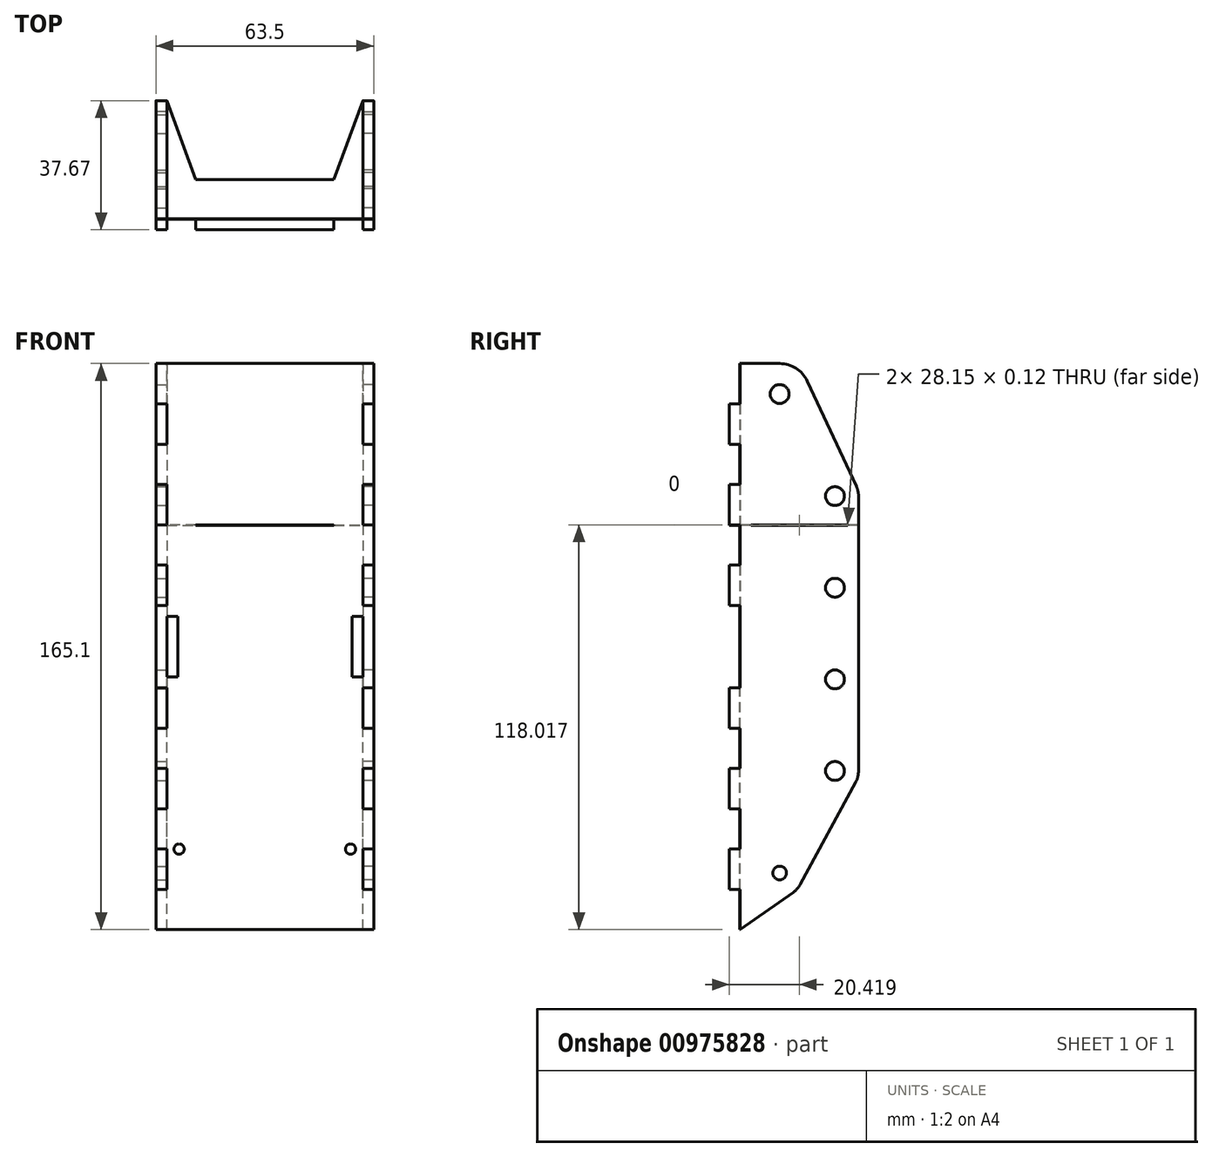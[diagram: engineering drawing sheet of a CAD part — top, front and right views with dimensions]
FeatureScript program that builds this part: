
annotation { "Feature Type Name" : "Feature", "Feature Type Description" : "" }
export const myFeature = defineFeature(function(context is Context, id is Id, definition is map)
    precondition{}
    {
        {
            assignVariable(context, id + "F0", {"name" : "Thickness", "anyValue" : .125});
        }
        {
            var Q0;
            Q0=qCreatedBy(makeId("Front.planeOp"),FACE);
            var sketch = newSketch(context, id + "F1", { "sketchPlane" : qUnion([Q0])});
            skLineSegment(sketch, "E0", {"start": v(0, 0) * mm, "end": v(0, 49.56) * mm, "construction": true});
            skLineSegment(sketch, "E1", {"start": v(0, 0) * mm, "end": v(-25, 0) * mm, "construction": true});
            skCircle(sketch, "E2", {"center": v(-25, 0) * mm, "radius": 1.5 * mm, "construction": true});
            skLineSegment(sketch, "E3", {"start": v(0, -7) * mm, "end": v(-39.83, -7) * mm, "construction": true});
            skLineSegment(sketch, "E4", {"start": v(0, 141.6) * mm, "end": v(-22.22, 141.6) * mm, "construction": true});
            skLineSegment(sketch, "E5", {"start": v(-22.23, 141.6) * mm, "end": v(-22.22, -23.51) * mm, "construction": true});
            skLineSegment(sketch, "E6", {"start": v(-22.22, -23.51) * mm, "end": v(0, -23.5) * mm, "construction": true});
            skSolve(sketch);
        }
        {
            var Q0;
            Q0=qCreatedBy(makeId("Right.planeOp"),FACE);
            var sketch = newSketch(context, id + "F2", { "sketchPlane" : qUnion([Q0])});
            skLineSegment(sketch, "E7", {"start": v(0, -7) * mm, "end": v(11.5, -7) * mm, "construction": true});
            skCircle(sketch, "E8", {"center": v(11.5, -7) * mm, "radius": 2 * mm});
            skCircle(sketch, "E9", {"center": v(11.5, 132.7) * mm, "radius": 2.75 * mm});
            skSolve(sketch);
        }
        {
            var Q0;
            Q0=qCreatedBy(makeId("Front.planeOp"),FACE);
            var sketch = newSketch(context, id + "F3", { "sketchPlane" : qUnion([Q0])});
            skLineSegment(sketch, "E10", {"start": v(0, 141.6) * mm, "end": v(-31.75, 141.6) * mm, "construction": true});
            skLineSegment(sketch, "E11", {"start": v(0, -23.51) * mm, "end": v(-31.75, -23.51) * mm});
            skLineSegment(sketch, "E12", {"start": v(-31.75, -23.51) * mm, "end": v(-31.75, -11.76) * mm});
            skLineSegment(sketch, "E13", {"start": v(-31.75, -11.76) * mm, "end": v(-28.57, -11.76) * mm});
            skLineSegment(sketch, "E14", {"start": v(-28.57, -11.76) * mm, "end": v(-28.57, 0) * mm});
            skLineSegment(sketch, "E15", {"start": v(-28.57, 0) * mm, "end": v(-31.75, 0) * mm});
            skLineSegment(sketch, "E16", {"start": v(0, -23.51) * mm, "end": v(0, 141.6) * mm, "construction": true});
            skLineSegment(sketch, "E17", {"start": v(0, 59.04) * mm, "end": v(-66.34, 59.04) * mm, "construction": true});
            skLineSegment(sketch, "E18", {"start": v(-31.75, 59.04) * mm, "end": v(-31.75, 47.02) * mm});
            skLineSegment(sketch, "E19.1.0.0", {"start": v(-28.57, 23.51) * mm, "end": v(-31.75, 23.51) * mm});
            skLineSegment(sketch, "E19.1.0.1", {"start": v(-28.57, 11.76) * mm, "end": v(-28.57, 23.51) * mm});
            skLineSegment(sketch, "E19.1.0.2", {"start": v(-31.75, 11.76) * mm, "end": v(-28.57, 11.76) * mm});
            skLineSegment(sketch, "E19.1.0.3", {"start": v(-31.75, 0) * mm, "end": v(-31.75, 11.76) * mm});
            skLineSegment(sketch, "E19.2.0.0", {"start": v(-28.58, 47.02) * mm, "end": v(-31.75, 47.02) * mm});
            skLineSegment(sketch, "E19.2.0.1", {"start": v(-28.57, 35.27) * mm, "end": v(-28.57, 47.02) * mm});
            skLineSegment(sketch, "E19.2.0.2", {"start": v(-31.75, 35.27) * mm, "end": v(-28.58, 35.27) * mm});
            skLineSegment(sketch, "E19.2.0.3", {"start": v(-31.75, 23.51) * mm, "end": v(-31.75, 35.27) * mm});
            skLineSegment(sketch, "E19.direction1", {"start": v(-31.75, -23.51) * mm, "end": v(-31.75, 0) * mm, "construction": true});
            skLineSegment(sketch, "E20.MirrorCS", {"start": v(-31.75, 141.6) * mm, "end": v(-31.75, 129.84) * mm});
            skLineSegment(sketch, "E21.MirrorCS", {"start": v(-28.57, 118.08) * mm, "end": v(-31.75, 118.08) * mm});
            skLineSegment(sketch, "E22.MirrorCS", {"start": v(-28.58, 71.06) * mm, "end": v(-31.75, 71.06) * mm});
            skLineSegment(sketch, "E23.MirrorCS", {"start": v(-31.75, 94.57) * mm, "end": v(-31.75, 82.81) * mm});
            skLineSegment(sketch, "E24.MirrorCS", {"start": v(-31.75, 118.08) * mm, "end": v(-31.75, 106.33) * mm});
            skLineSegment(sketch, "E25.MirrorCS", {"start": v(-31.75, 129.84) * mm, "end": v(-28.57, 129.84) * mm});
            skLineSegment(sketch, "E26.MirrorCS", {"start": v(-28.57, 129.84) * mm, "end": v(-28.57, 118.08) * mm});
            skLineSegment(sketch, "E27.MirrorCS", {"start": v(-28.57, 82.81) * mm, "end": v(-28.57, 71.06) * mm});
            skLineSegment(sketch, "E28.MirrorCS", {"start": v(-31.75, 82.81) * mm, "end": v(-28.58, 82.81) * mm});
            skLineSegment(sketch, "E29.MirrorCS", {"start": v(-31.75, 106.33) * mm, "end": v(-28.57, 106.33) * mm});
            skLineSegment(sketch, "E30.MirrorCS", {"start": v(-28.57, 106.33) * mm, "end": v(-28.57, 94.57) * mm});
            skLineSegment(sketch, "E31.MirrorCS", {"start": v(-28.57, 94.57) * mm, "end": v(-31.75, 94.57) * mm});
            skLineSegment(sketch, "E32.MirrorCS", {"start": v(0, 141.6) * mm, "end": v(-31.75, 141.6) * mm});
            skLineSegment(sketch, "E33.MirrorCS", {"start": v(-31.75, 59.04) * mm, "end": v(-31.75, 71.06) * mm});
            skLineSegment(sketch, "E34.bottom", {"start": v(-28.58, 67.89) * mm, "end": v(-25.4, 67.89) * mm});
            skLineSegment(sketch, "E34.top", {"start": v(-28.58, 50.2) * mm, "end": v(-25.4, 50.2) * mm});
            skLineSegment(sketch, "E34.left", {"start": v(-28.58, 67.89) * mm, "end": v(-28.58, 50.2) * mm});
            skLineSegment(sketch, "E34.right", {"start": v(-25.4, 67.89) * mm, "end": v(-25.4, 50.2) * mm});
            skPoint(sketch, "E35", {"position": v(-28.58, 59.04) * mm});
            skLineSegment(sketch, "E36.MirrorCS", {"start": v(28.57, 23.51) * mm, "end": v(31.75, 23.51) * mm});
            skLineSegment(sketch, "E37.MirrorCS", {"start": v(31.75, 35.27) * mm, "end": v(28.58, 35.27) * mm});
            skLineSegment(sketch, "E38.MirrorCS", {"start": v(28.58, 71.06) * mm, "end": v(31.75, 71.06) * mm});
            skLineSegment(sketch, "E39.MirrorCS", {"start": v(31.75, -23.51) * mm, "end": v(31.75, -11.76) * mm});
            skLineSegment(sketch, "E40.MirrorCS", {"start": v(28.57, 0) * mm, "end": v(31.75, 0) * mm});
            skLineSegment(sketch, "E41.MirrorCS", {"start": v(28.58, 67.89) * mm, "end": v(25.4, 67.89) * mm});
            skLineSegment(sketch, "E42.MirrorCS", {"start": v(31.75, 82.81) * mm, "end": v(28.58, 82.81) * mm});
            skLineSegment(sketch, "E43.MirrorCS", {"start": v(31.75, 59.04) * mm, "end": v(31.75, 71.06) * mm});
            skLineSegment(sketch, "E44.MirrorCS", {"start": v(31.75, 11.76) * mm, "end": v(28.57, 11.76) * mm});
            skLineSegment(sketch, "E45.MirrorCS", {"start": v(31.75, 94.57) * mm, "end": v(31.75, 82.81) * mm});
            skLineSegment(sketch, "E46.MirrorCS", {"start": v(31.75, 141.6) * mm, "end": v(31.75, 129.84) * mm});
            skLineSegment(sketch, "E47.MirrorCS", {"start": v(28.57, 94.57) * mm, "end": v(31.75, 94.57) * mm});
            skLineSegment(sketch, "E48.MirrorCS", {"start": v(31.75, 118.08) * mm, "end": v(31.75, 106.33) * mm});
            skLineSegment(sketch, "E49.MirrorCS", {"start": v(31.75, -11.76) * mm, "end": v(28.57, -11.76) * mm});
            skLineSegment(sketch, "E50.MirrorCS", {"start": v(28.57, 118.08) * mm, "end": v(31.75, 118.08) * mm});
            skLineSegment(sketch, "E51.MirrorCS", {"start": v(31.75, 23.51) * mm, "end": v(31.75, 35.27) * mm});
            skLineSegment(sketch, "E52.MirrorCS", {"start": v(28.57, -11.76) * mm, "end": v(28.57, 0) * mm});
            skLineSegment(sketch, "E53.MirrorCS", {"start": v(31.75, 129.84) * mm, "end": v(28.57, 129.84) * mm});
            skLineSegment(sketch, "E54.MirrorCS", {"start": v(28.58, 67.89) * mm, "end": v(28.58, 50.2) * mm});
            skLineSegment(sketch, "E55.MirrorCS", {"start": v(28.58, 47.02) * mm, "end": v(31.75, 47.02) * mm});
            skLineSegment(sketch, "E56.MirrorCS", {"start": v(28.57, 35.27) * mm, "end": v(28.57, 47.02) * mm});
            skLineSegment(sketch, "E57.MirrorCS", {"start": v(31.75, 0) * mm, "end": v(31.75, 11.76) * mm});
            skLineSegment(sketch, "E58.MirrorCS", {"start": v(31.75, 59.04) * mm, "end": v(31.75, 47.02) * mm});
            skLineSegment(sketch, "E59.MirrorCS", {"start": v(28.57, 11.76) * mm, "end": v(28.57, 23.51) * mm});
            skLineSegment(sketch, "E60.MirrorCS", {"start": v(28.58, 50.2) * mm, "end": v(25.4, 50.2) * mm});
            skLineSegment(sketch, "E61.MirrorCS", {"start": v(31.75, 106.33) * mm, "end": v(28.57, 106.33) * mm});
            skLineSegment(sketch, "E62.MirrorCS", {"start": v(28.57, 82.81) * mm, "end": v(28.57, 71.06) * mm});
            skLineSegment(sketch, "E63.MirrorCS", {"start": v(28.57, 129.84) * mm, "end": v(28.57, 118.08) * mm});
            skLineSegment(sketch, "E64.MirrorCS", {"start": v(28.57, 106.33) * mm, "end": v(28.57, 94.57) * mm});
            skLineSegment(sketch, "E65.MirrorCS", {"start": v(0, 141.6) * mm, "end": v(31.75, 141.6) * mm});
            skLineSegment(sketch, "E66.MirrorCS", {"start": v(25.4, 67.89) * mm, "end": v(25.4, 50.2) * mm});
            skLineSegment(sketch, "E67.MirrorCS", {"start": v(0, 141.6) * mm, "end": v(31.75, 141.6) * mm, "construction": true});
            skLineSegment(sketch, "E68.MirrorCS", {"start": v(0, -23.51) * mm, "end": v(31.75, -23.51) * mm});
            skPoint(sketch, "E69.MirrorP", {"position": v(28.58, 59.04) * mm});
            skCircle(sketch, "E70", {"center": v(-25, 0) * mm, "radius": 1.5 * mm});
            skCircle(sketch, "E71.MirrorC", {"center": v(25, 0) * mm, "radius": 1.5 * mm});
            skSolve(sketch);
        }
        {
            var Q0;
            Q0=makeQuery(id+"F3.imprint","IMPRINT",FACE,{"disambiguationData":[TD([[makeQuery(id+"F3.imprint","IMPRINT",EDGE,{"derivedFrom":sQuery(id+"F3.wireOp",EDGE,"E11")}),-1.0]])]});
            extrude(context, id + "F4", {"entities" : qUnion([Q0]), "depth" : (getVariable(context, 'Thickness')) * mm, "offsetDistance" : 25.4 * mm});
        }
        {
            var Q0;
            Q0=qCreatedBy(makeId("Right.planeOp"),FACE);
            var sketch = newSketch(context, id + "F5", { "sketchPlane" : qUnion([Q0])});
            skLineSegment(sketch, "E72", {"start": v(0, -23.51) * mm, "end": v(0, -11.76) * mm});
            skLineSegment(sketch, "E73", {"start": v(0, -11.76) * mm, "end": v(-3.18, -11.76) * mm});
            skLineSegment(sketch, "E74", {"start": v(-3.18, -11.76) * mm, "end": v(-3.18, 0) * mm});
            skLineSegment(sketch, "E75", {"start": v(-3.18, 0) * mm, "end": v(0, 0) * mm});
            skLineSegment(sketch, "E76.1.0.0", {"start": v(0, 0) * mm, "end": v(0, 11.75) * mm});
            skLineSegment(sketch, "E76.1.0.1", {"start": v(0, 11.76) * mm, "end": v(-3.18, 11.75) * mm});
            skLineSegment(sketch, "E76.1.0.2", {"start": v(-3.18, 11.75) * mm, "end": v(-3.18, 23.51) * mm});
            skLineSegment(sketch, "E76.1.0.3", {"start": v(-3.18, 23.51) * mm, "end": v(0, 23.51) * mm});
            skLineSegment(sketch, "E76.2.0.0", {"start": v(0, 23.51) * mm, "end": v(0, 35.27) * mm});
            skLineSegment(sketch, "E76.2.0.1", {"start": v(0, 35.27) * mm, "end": v(-3.17, 35.27) * mm});
            skLineSegment(sketch, "E76.2.0.2", {"start": v(-3.17, 35.27) * mm, "end": v(-3.17, 47.02) * mm});
            skLineSegment(sketch, "E76.2.0.3", {"start": v(-3.17, 47.02) * mm, "end": v(0, 47.02) * mm});
            skLineSegment(sketch, "E76.direction1", {"start": v(0, -23.51) * mm, "end": v(0, 0) * mm, "construction": true});
            skLineSegment(sketch, "E77", {"start": v(-17.44, 59.04) * mm, "end": v(0, 59.04) * mm, "construction": true});
            skLineSegment(sketch, "E78", {"start": v(0, 47.02) * mm, "end": v(0, 59.04) * mm});
            skLineSegment(sketch, "E79.MirrorCS", {"start": v(-3.18, 118.08) * mm, "end": v(0, 118.08) * mm});
            skLineSegment(sketch, "E80.MirrorCS", {"start": v(0, 82.82) * mm, "end": v(-3.17, 82.82) * mm});
            skLineSegment(sketch, "E81.MirrorCS", {"start": v(-3.18, 94.57) * mm, "end": v(0, 94.57) * mm});
            skLineSegment(sketch, "E82.MirrorCS", {"start": v(0, 129.84) * mm, "end": v(-3.18, 129.84) * mm});
            skLineSegment(sketch, "E83.MirrorCS", {"start": v(-3.17, 71.06) * mm, "end": v(0, 71.06) * mm});
            skLineSegment(sketch, "E84.MirrorCS", {"start": v(0, 106.33) * mm, "end": v(-3.18, 106.33) * mm});
            skLineSegment(sketch, "E85.MirrorCS", {"start": v(0, 141.6) * mm, "end": v(0, 129.84) * mm});
            skLineSegment(sketch, "E86.MirrorCS", {"start": v(0, 141.6) * mm, "end": v(0, 118.08) * mm, "construction": true});
            skLineSegment(sketch, "E87.MirrorCS", {"start": v(-3.18, 106.33) * mm, "end": v(-3.18, 94.57) * mm});
            skLineSegment(sketch, "E88.MirrorCS", {"start": v(0, 118.08) * mm, "end": v(0, 106.33) * mm});
            skLineSegment(sketch, "E89.MirrorCS", {"start": v(-3.17, 82.82) * mm, "end": v(-3.17, 71.06) * mm});
            skLineSegment(sketch, "E90.MirrorCS", {"start": v(0, 71.06) * mm, "end": v(0, 59.04) * mm});
            skLineSegment(sketch, "E91.MirrorCS", {"start": v(0, 94.57) * mm, "end": v(0, 82.82) * mm});
            skLineSegment(sketch, "E92.MirrorCS", {"start": v(-3.18, 129.84) * mm, "end": v(-3.18, 118.08) * mm});
            skLineSegment(sketch, "E93", {"start": v(0, 141.6) * mm, "end": v(11.5, 141.6) * mm});
            skLineSegment(sketch, "E94", {"start": v(0, -23.51) * mm, "end": v(15.45, -12.6) * mm});
            skArc(sketch, "E95", {"start": v(11.5, 141.6) * mm, "mid": v(16.28, 140.2) * mm, "end": v(19.56, 136.46) * mm});
            skCircle(sketch, "E96", {"center": v(11.5, 132.7) * mm, "radius": 2.75 * mm});
            skCircle(sketch, "E97", {"center": v(11.5, -7) * mm, "radius": 2 * mm});
            skArc(sketch, "E98", {"start": v(15.45, -12.6) * mm, "mid": v(16.63, -11.56) * mm, "end": v(17.53, -10.27) * mm});
            skLineSegment(sketch, "E99", {"start": v(19.56, 136.46) * mm, "end": v(33.85, 105.83) * mm});
            skLineSegment(sketch, "E100", {"start": v(17.53, -10.27) * mm, "end": v(33.67, 19.5) * mm});
            skLineSegment(sketch, "E101", {"start": v(34.5, 102.93) * mm, "end": v(34.5, 22.77) * mm});
            skArc(sketch, "E102", {"start": v(33.67, 19.5) * mm, "mid": v(34.29, 21.09) * mm, "end": v(34.5, 22.77) * mm});
            skArc(sketch, "E103", {"start": v(33.85, 105.83) * mm, "mid": v(34.33, 104.41) * mm, "end": v(34.5, 102.93) * mm});
            skCircle(sketch, "E104", {"center": v(11.5, 132.7) * mm, "radius": 16 * mm, "construction": true});
            skCircle(sketch, "E105", {"center": v(11.5, -7) * mm, "radius": 16 * mm, "construction": true});
            skCircle(sketch, "E106", {"center": v(27.64, 22.77) * mm, "radius": 11 * mm, "construction": true});
            skCircle(sketch, "E107", {"center": v(27.64, 102.93) * mm, "radius": 11 * mm, "construction": true});
            skLineSegment(sketch, "E108", {"start": v(38.64, 102.93) * mm, "end": v(38.64, 22.77) * mm, "construction": true});
            skCircle(sketch, "E109.1.0.0", {"center": v(27.64, 76.2) * mm, "radius": 11 * mm, "construction": true});
            skCircle(sketch, "E109.2.0.0", {"center": v(27.64, 49.5) * mm, "radius": 11 * mm, "construction": true});
            skLineSegment(sketch, "E109.direction1", {"start": v(27.64, 102.93) * mm, "end": v(27.64, 76.2) * mm, "construction": true});
            skLineSegment(sketch, "E110", {"start": v(27.64, 49.5) * mm, "end": v(27.64, 22.77) * mm, "construction": true});
            skCircle(sketch, "E111", {"center": v(27.64, 102.93) * mm, "radius": 2.75 * mm});
            skCircle(sketch, "E112", {"center": v(27.64, 76.2) * mm, "radius": 2.75 * mm});
            skCircle(sketch, "E113", {"center": v(27.64, 49.5) * mm, "radius": 2.75 * mm});
            skCircle(sketch, "E114", {"center": v(27.64, 22.77) * mm, "radius": 2.75 * mm});
            skSolve(sketch);
        }
        {
            var Q0;
            Q0=makeQuery(id+"F5.imprint","IMPRINT",FACE,{"disambiguationData":[TD([[makeQuery(id+"F5.imprint","IMPRINT",EDGE,{"derivedFrom":sQuery(id+"F5.wireOp",EDGE,"E72")}),-1.0]])]});
            var Q1;
            Q1=makeQuery(id+"F4.opExtrude","CAP_VERTEX",VERTEX,{"disambiguationData":[OSD([sQuery(id+"F3.wireOp",EDGE,"E46.MirrorCS"),sQuery(id+"F3.wireOp",EDGE,"E65.MirrorCS")])],"isStart":false});
            var Q2;
            Q2=makeQuery(id+"F4.opExtrude","CAP_VERTEX",VERTEX,{"disambiguationData":[OSD([sQuery(id+"F3.wireOp",EDGE,"E53.MirrorCS"),sQuery(id+"F3.wireOp",EDGE,"E63.MirrorCS")])],"isStart":true});
            extrude(context, id + "F6", {"entities" : qUnion([Q0]), "endBound" : BoundingType.UP_TO_VERTEX, "depth" : 25.4 * mm, "endBoundEntityVertex" : qUnion([Q1]), "offsetDistance" : 25.4 * mm, "hasSecondDirection" : true, "secondDirectionBound" : SecondDirectionBoundingType.UP_TO_VERTEX, "secondDirectionOppositeDirection" : false, "secondDirectionDepth" : 25.4 * mm, "secondDirectionBoundEntityVertex" : qUnion([Q2])});
        }
        {
            var Q0;
            Q0=makeQuery(id+"F6.opExtrude","SWEPT_BODY",BODY,{"disambiguationData":[OSD([sQuery(id+"F5.wireOp",EDGE,"E72"),sQuery(id+"F5.wireOp",EDGE,"E73"),sQuery(id+"F5.wireOp",EDGE,"E74"),sQuery(id+"F5.wireOp",EDGE,"E75"),sQuery(id+"F5.wireOp",EDGE,"E76.1.0.0"),sQuery(id+"F5.wireOp",EDGE,"E76.1.0.1"),sQuery(id+"F5.wireOp",EDGE,"E76.1.0.2"),sQuery(id+"F5.wireOp",EDGE,"E76.1.0.3"),sQuery(id+"F5.wireOp",EDGE,"E76.2.0.0"),sQuery(id+"F5.wireOp",EDGE,"E76.2.0.1"),sQuery(id+"F5.wireOp",EDGE,"E76.2.0.2"),sQuery(id+"F5.wireOp",EDGE,"E76.2.0.3"),sQuery(id+"F5.wireOp",EDGE,"E78"),sQuery(id+"F5.wireOp",EDGE,"E79.MirrorCS"),sQuery(id+"F5.wireOp",EDGE,"E80.MirrorCS"),sQuery(id+"F5.wireOp",EDGE,"E81.MirrorCS"),sQuery(id+"F5.wireOp",EDGE,"E82.MirrorCS"),sQuery(id+"F5.wireOp",EDGE,"E83.MirrorCS"),sQuery(id+"F5.wireOp",EDGE,"E84.MirrorCS"),sQuery(id+"F5.wireOp",EDGE,"E85.MirrorCS"),sQuery(id+"F5.wireOp",EDGE,"E87.MirrorCS"),sQuery(id+"F5.wireOp",EDGE,"E88.MirrorCS"),sQuery(id+"F5.wireOp",EDGE,"E89.MirrorCS"),sQuery(id+"F5.wireOp",EDGE,"E90.MirrorCS"),sQuery(id+"F5.wireOp",EDGE,"E91.MirrorCS"),sQuery(id+"F5.wireOp",EDGE,"E92.MirrorCS"),sQuery(id+"F5.wireOp",EDGE,"E93"),sQuery(id+"F5.wireOp",EDGE,"E94"),sQuery(id+"F5.wireOp",EDGE,"pLrTUgb4-zpkk-BDbY-rqmu-NSZ4KMZ8J1Q6"),sQuery(id+"F5.wireOp",EDGE,"E95"),sQuery(id+"F5.wireOp",EDGE,"E96"),sQuery(id+"F5.wireOp",EDGE,"E97"),sQuery(id+"F5.wireOp",EDGE,"E98")])]});
            var Q1;
            Q1=qCreatedBy(makeId("Right.planeOp"),FACE);
            mirror(context, id + "F7", {"entities" : qUnion([Q0]), "mirrorPlane" : qUnion([Q1])});
        }
        {
            var Q0;
            Q0=qCreatedBy(makeId("Top.planeOp"),FACE);
            var sketch = newSketch(context, id + "F8", { "sketchPlane" : qUnion([Q0])});
            skLineSegment(sketch, "E115", {"start": v(0, 11.5) * mm, "end": v(-20.1, 11.5) * mm});
            skLineSegment(sketch, "E116", {"start": v(-20.1, 11.5) * mm, "end": v(-28.57, 34.5) * mm});
            skLineSegment(sketch, "E117", {"start": v(-28.57, 34.5) * mm, "end": v(-28.57, 31.32) * mm});
            skLineSegment(sketch, "E118", {"start": v(-28.57, 31.32) * mm, "end": v(-31.75, 31.32) * mm});
            skLineSegment(sketch, "E119", {"start": v(-31.75, 31.32) * mm, "end": v(-31.75, 3.17) * mm});
            skLineSegment(sketch, "E120", {"start": v(-31.75, 3.17) * mm, "end": v(-28.57, 3.17) * mm});
            skLineSegment(sketch, "E121", {"start": v(-28.57, 3.18) * mm, "end": v(-28.57, 0) * mm});
            skLineSegment(sketch, "E122", {"start": v(-28.57, 0) * mm, "end": v(-20.1, 0) * mm});
            skLineSegment(sketch, "E123", {"start": v(-20.1, 0) * mm, "end": v(-20.1, -3.18) * mm});
            skLineSegment(sketch, "E124", {"start": v(-20.1, -3.18) * mm, "end": v(0, -3.18) * mm});
            skLineSegment(sketch, "E125", {"start": v(0, -3.18) * mm, "end": v(0, 11.5) * mm, "construction": true});
            skLineSegment(sketch, "E126.MirrorCS", {"start": v(20.1, 0) * mm, "end": v(20.1, -3.17) * mm});
            skLineSegment(sketch, "E127.MirrorCS", {"start": v(28.57, 3.18) * mm, "end": v(28.57, 0) * mm});
            skLineSegment(sketch, "E128.MirrorCS", {"start": v(28.57, 0) * mm, "end": v(20.1, 0) * mm});
            skLineSegment(sketch, "E129.MirrorCS", {"start": v(28.57, 34.5) * mm, "end": v(28.57, 31.32) * mm});
            skLineSegment(sketch, "E130.MirrorCS", {"start": v(28.57, 31.32) * mm, "end": v(31.75, 31.32) * mm});
            skLineSegment(sketch, "E131.MirrorCS", {"start": v(31.75, 3.17) * mm, "end": v(28.57, 3.17) * mm});
            skLineSegment(sketch, "E132.MirrorCS", {"start": v(0, 11.5) * mm, "end": v(20.1, 11.5) * mm});
            skLineSegment(sketch, "E133.MirrorCS", {"start": v(20.1, -3.18) * mm, "end": v(0, -3.18) * mm});
            skLineSegment(sketch, "E134.MirrorCS", {"start": v(20.1, 11.5) * mm, "end": v(28.57, 34.5) * mm});
            skLineSegment(sketch, "E135.MirrorCS", {"start": v(31.75, 31.32) * mm, "end": v(31.75, 3.18) * mm});
            skSolve(sketch);
        }
        {
            var Q0;
            Q0=qSketchRegion(id+"F8",true);
            var Q1;
            Q1=makeQuery(id+"F4.opExtrude","CAP_VERTEX",VERTEX,{"disambiguationData":[OSD([sQuery(id+"F3.wireOp",EDGE,"E23.MirrorCS"),sQuery(id+"F3.wireOp",EDGE,"E31.MirrorCS")])],"isStart":true});
            var Q2;
            Q2=makeQuery(id+"F4.opExtrude","CAP_VERTEX",VERTEX,{"disambiguationData":[OSD([sQuery(id+"F3.wireOp",EDGE,"E23.MirrorCS"),sQuery(id+"F3.wireOp",EDGE,"E31.MirrorCS")])],"isStart":true});
            extrude(context, id + "F9", {"entities" : qUnion([Q0]), "operationType" : NewBodyOperationType.REMOVE, "endBound" : BoundingType.UP_TO_VERTEX, "depth" : 25.4 * mm, "endBoundEntityVertex" : qUnion([Q1]), "offsetDistance" : 25.4 * mm, "hasSecondDirection" : true, "secondDirectionBound" : SecondDirectionBoundingType.UP_TO_VERTEX, "secondDirectionOppositeDirection" : false, "secondDirectionDepth" : 25.4 * mm, "secondDirectionBoundEntityVertex" : qUnion([Q2]), "hasSecondDirectionOffset" : true, "secondDirectionOffsetDistance" : (getVariable(context, 'Thickness')) * mm});
        }
        {
            var Q0;
            Q0=qSketchRegion(id+"F8",true);
            var Q1;
            Q1=makeQuery(id+"F4.opExtrude","CAP_VERTEX",VERTEX,{"disambiguationData":[OSD([sQuery(id+"F3.wireOp",EDGE,"E23.MirrorCS"),sQuery(id+"F3.wireOp",EDGE,"E31.MirrorCS")])],"isStart":true});
            var Q2;
            Q2=makeQuery(id+"F4.opExtrude","CAP_VERTEX",VERTEX,{"disambiguationData":[OSD([sQuery(id+"F3.wireOp",EDGE,"E23.MirrorCS"),sQuery(id+"F3.wireOp",EDGE,"E31.MirrorCS")])],"isStart":true});
            extrude(context, id + "F10", {"entities" : qUnion([Q0]), "endBound" : BoundingType.UP_TO_VERTEX, "depth" : 25.4 * mm, "endBoundEntityVertex" : qUnion([Q1]), "offsetDistance" : 25.4 * mm, "hasSecondDirection" : true, "secondDirectionBound" : SecondDirectionBoundingType.UP_TO_VERTEX, "secondDirectionOppositeDirection" : false, "secondDirectionDepth" : 25.4 * mm, "secondDirectionBoundEntityVertex" : qUnion([Q2]), "hasSecondDirectionOffset" : true, "secondDirectionOffsetDistance" : (getVariable(context, 'Thickness')) * mm});
        }
    });
